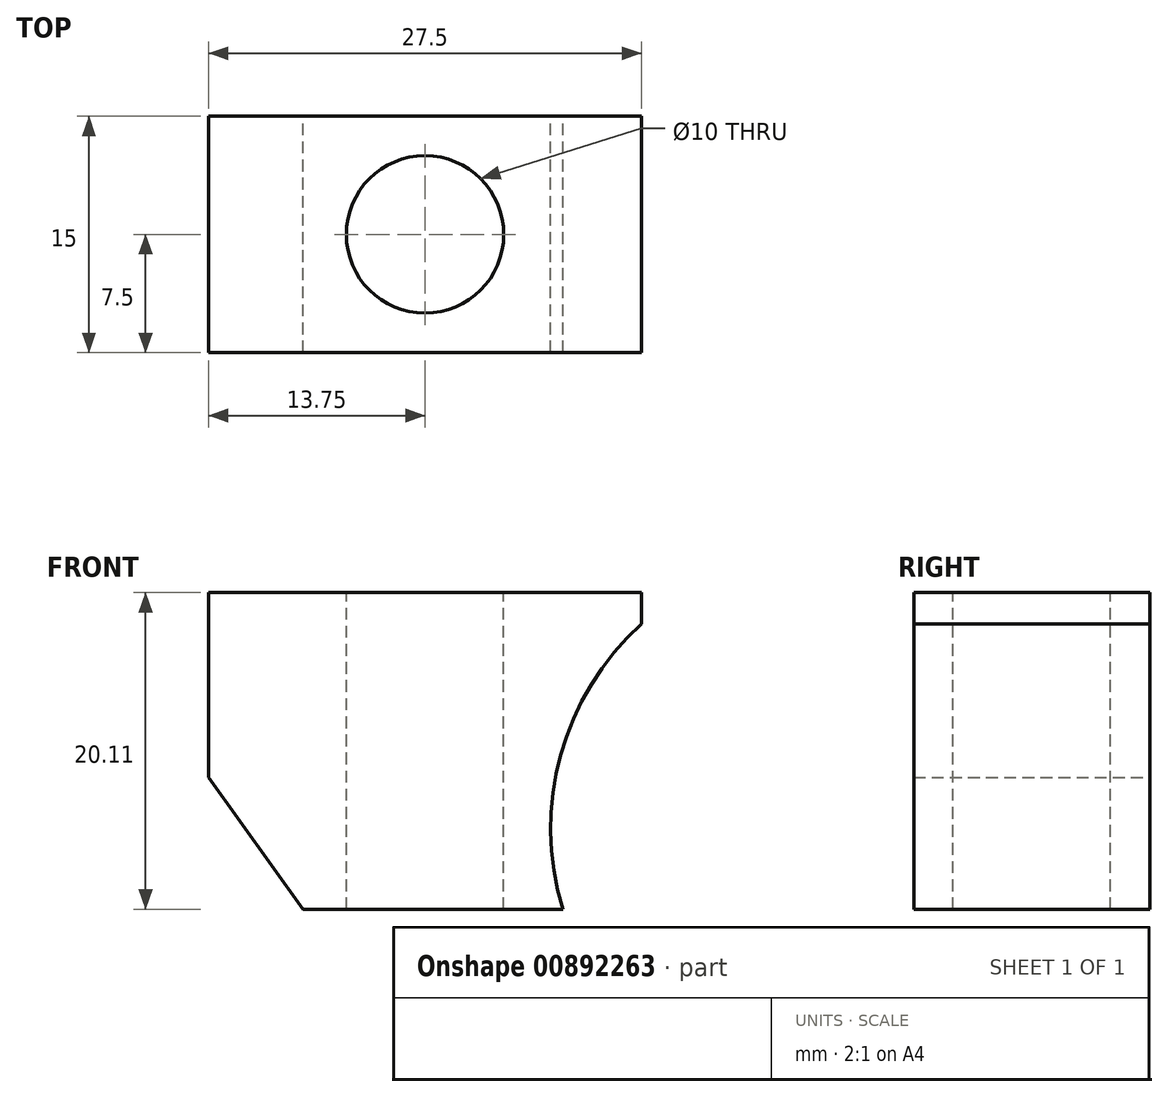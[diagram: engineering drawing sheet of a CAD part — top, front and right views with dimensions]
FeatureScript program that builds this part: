
annotation { "Feature Type Name" : "Feature", "Feature Type Description" : "" }
export const myFeature = defineFeature(function(context is Context, id is Id, definition is map)
    precondition{}
    {
        {
            var Q0;
            Q0=qCreatedBy(makeId("Front.planeOp"),FACE);
            var sketch = newSketch(context, id + "F0", { "sketchPlane" : qUnion([Q0])});
            skLineSegment(sketch, "E0", {"start": v(-6, 11.75) * mm, "end": v(21.5, 11.75) * mm});
            skLineSegment(sketch, "E1", {"start": v(-6, 11.75) * mm, "end": v(-6, 0) * mm});
            skLineSegment(sketch, "E2", {"start": v(-6, 0) * mm, "end": v(0, -8.36) * mm});
            skLineSegment(sketch, "E3", {"start": v(0, -8.36) * mm, "end": v(16.5, -8.36) * mm});
            skLineSegment(sketch, "E4", {"start": v(21.5, 11.75) * mm, "end": v(21.5, 9.75) * mm});
            skArc(sketch, "E5", {"start": v(21.5, 9.75) * mm, "mid": v(16.36, 1.42) * mm, "end": v(16.5, -8.36) * mm});
            skSolve(sketch);
        }
        {
            var Q0;
            Q0=makeQuery(id+"F0.imprint","IMPRINT",FACE,{"disambiguationData":[TD([[makeQuery(id+"F0.imprint","IMPRINT",EDGE,{"derivedFrom":sQuery(id+"F0.wireOp",EDGE,"E0")}),-1.0]])]});
            extrude(context, id + "F1", {"entities" : qUnion([Q0]), "depth" : 15 * mm, "offsetDistance" : 25.4 * mm});
        }
        {
            var Q0;
            Q0=makeQuery(id+"F1.opExtrude","SWEPT_FACE",FACE,{"disambiguationData":[OSD([sQuery(id+"F0.wireOp",EDGE,"E0")])]});
            var sketch = newSketch(context, id + "F2", { "sketchPlane" : qUnion([Q0])});
            skPoint(sketch, "E6", {"position": v(7.75, -7.5) * mm});
            skPoint(sketch, "E6.positionSnap0", {"position": v(-6, -7.5) * mm});
            skPoint(sketch, "E6.positionSnap1", {"position": v(7.75, 0) * mm});
            skSolve(sketch);
        }
        {
            var Q0;
            Q0=sQuery(id+"F2.wireOp",VERTEX,"E6");
            var Q1;
            Q1=makeQuery(id+"F1.opExtrude","SWEPT_BODY",BODY,{"disambiguationData":[OSD([sQuery(id+"F0.wireOp",EDGE,"E0"),sQuery(id+"F0.wireOp",EDGE,"E1"),sQuery(id+"F0.wireOp",EDGE,"E2"),sQuery(id+"F0.wireOp",EDGE,"E3"),sQuery(id+"F0.wireOp",EDGE,"E4"),sQuery(id+"F0.wireOp",EDGE,"E5")])]});
            hole(context, id + "F3", {"style" : HoleStyle.C_BORE, "endStyle" : HoleEndStyle.THROUGH, "holeDiameter" : 7.5 * mm, "cBoreDiameter" : 10 * mm, "cBoreDepth" : 44 * mm, "majorDiameter" : 5 * mm, "isTappedThrough" : true, "tappedDepth" : 12 * mm, "tapClearance" : 3, "locations" : qUnion([Q0]), "scope" : qUnion([Q1])});
        }
    });
